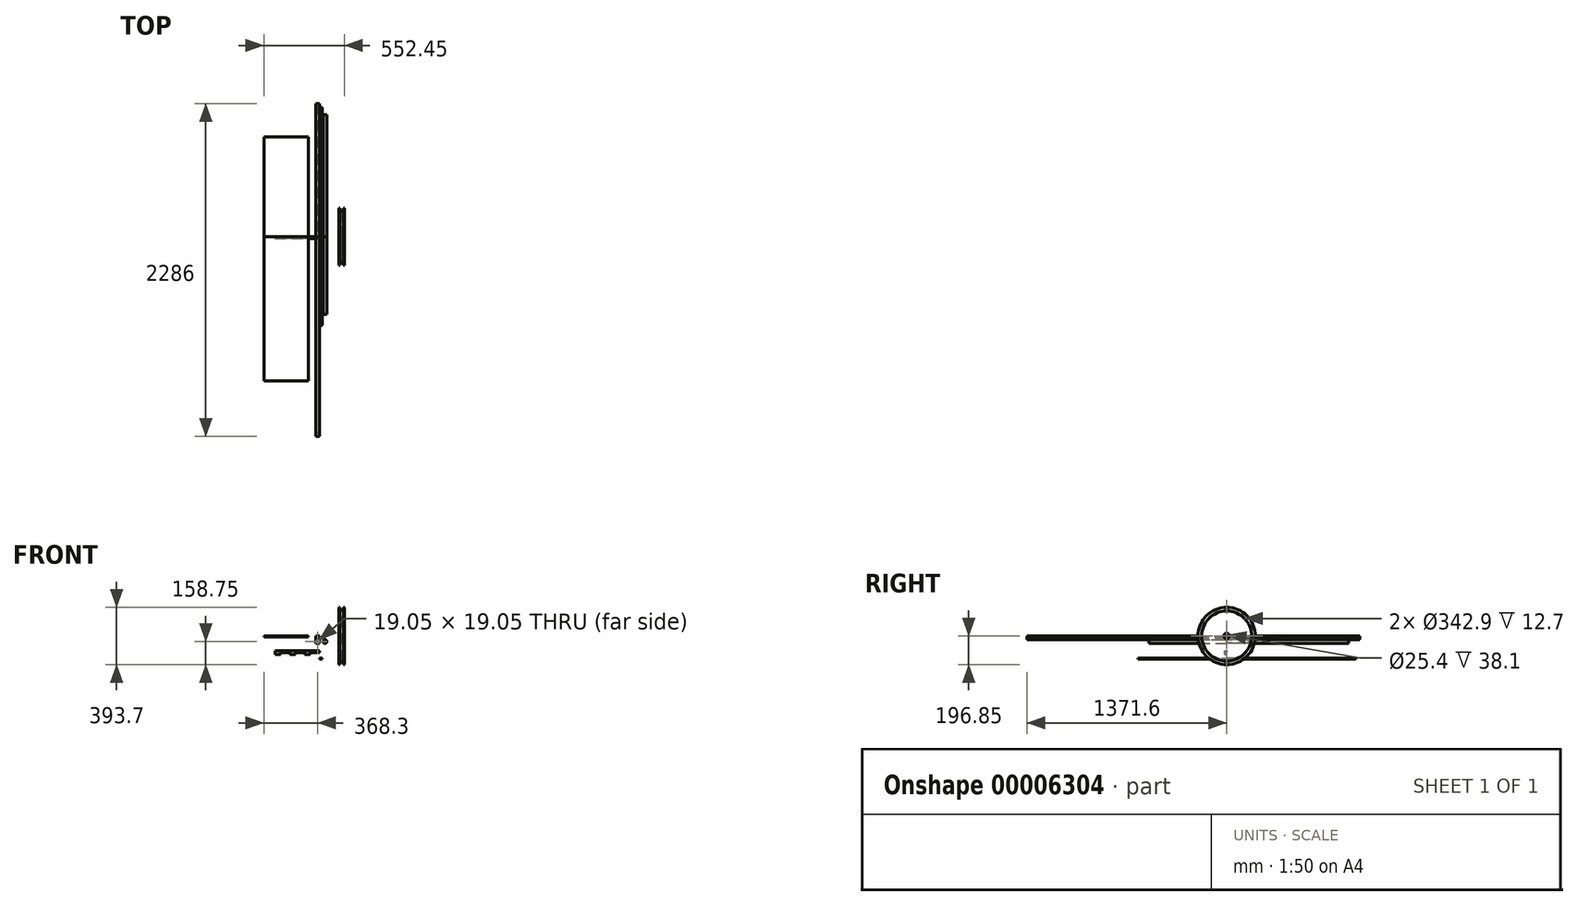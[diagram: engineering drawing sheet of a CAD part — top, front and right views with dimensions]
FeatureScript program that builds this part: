
annotation { "Feature Type Name" : "Feature", "Feature Type Description" : "" }
export const myFeature = defineFeature(function(context is Context, id is Id, definition is map)
    precondition{}
    {
        {
            var Q0;
            Q0=qCreatedBy(makeId("Front.planeOp"),FACE);
            var sketch = newSketch(context, id + "F0", { "sketchPlane" : qUnion([Q0])});
            skLineSegment(sketch, "E0", {"start": v(-25.4, 0) * mm, "end": v(-25.4, -25.4) * mm});
            skLineSegment(sketch, "E1", {"start": v(-25.4, -25.4) * mm, "end": v(-25.4, -25.4) * mm});
            skLineSegment(sketch, "E2", {"start": v(0, -19.05) * mm, "end": v(-19.05, -19.05) * mm});
            skLineSegment(sketch, "E3", {"start": v(-19.05, -25.4) * mm, "end": v(-19.05, -6.35) * mm});
            skLineSegment(sketch, "E4", {"start": v(-19.05, -6.35) * mm, "end": v(0, -6.35) * mm});
            skLineSegment(sketch, "E5", {"start": v(0, -25.4) * mm, "end": v(0, -19.05) * mm});
            skLineSegment(sketch, "E6", {"start": v(0, 0) * mm, "end": v(-25.4, 0) * mm});
            skLineSegment(sketch, "E7", {"start": v(0, 0) * mm, "end": v(0, -6.35) * mm});
            skLineSegment(sketch, "E8", {"start": v(-25.4, -25.4) * mm, "end": v(0, -25.4) * mm});
            skLineSegment(sketch, "E9", {"start": v(0, -25.4) * mm, "end": v(0, -50.8) * mm});
            skLineSegment(sketch, "E10", {"start": v(0, -50.8) * mm, "end": v(-25.4, -50.8) * mm});
            skLineSegment(sketch, "E11", {"start": v(-25.4, -50.8) * mm, "end": v(-25.4, -25.4) * mm});
            skLineSegment(sketch, "E12", {"start": v(-22.22, -28.57) * mm, "end": v(-22.22, -47.62) * mm});
            skLineSegment(sketch, "E13", {"start": v(-22.22, -47.62) * mm, "end": v(-3.17, -47.62) * mm});
            skLineSegment(sketch, "E14", {"start": v(-3.17, -47.62) * mm, "end": v(-3.18, -28.57) * mm});
            skLineSegment(sketch, "E15", {"start": v(-3.18, -28.57) * mm, "end": v(-22.22, -28.57) * mm});
            skCircle(sketch, "E16.0", {"center": v(38.1, -38.1) * mm, "radius": 12.7 * mm});
            skLineSegment(sketch, "E17.bottom", {"start": v(-76.2, 0) * mm, "end": v(-381, 0) * mm});
            skLineSegment(sketch, "E17.top", {"start": v(-76.2, -6.35) * mm, "end": v(-381, -6.35) * mm});
            skLineSegment(sketch, "E17.left", {"start": v(-76.2, 0) * mm, "end": v(-76.2, -6.35) * mm});
            skLineSegment(sketch, "E17.right", {"start": v(-381, 0) * mm, "end": v(-381, -6.35) * mm});
            skLineSegment(sketch, "E18", {"start": v(-304.8, -127) * mm, "end": v(-304.8, -101.6) * mm});
            skLineSegment(sketch, "E19", {"start": v(-304.8, -101.6) * mm, "end": v(0, -101.6) * mm});
            skLineSegment(sketch, "E20", {"start": v(0, -101.6) * mm, "end": v(0, -114.3) * mm});
            skLineSegment(sketch, "E21", {"start": v(0, -114.3) * mm, "end": v(-63.5, -114.3) * mm});
            skLineSegment(sketch, "E22", {"start": v(-63.5, -127) * mm, "end": v(-63.5, -114.3) * mm});
            skLineSegment(sketch, "E23", {"start": v(-63.5, -127) * mm, "end": v(-101.6, -127) * mm});
            skLineSegment(sketch, "E24", {"start": v(-101.6, -114.3) * mm, "end": v(-101.6, -127) * mm});
            skLineSegment(sketch, "E25", {"start": v(-101.6, -114.3) * mm, "end": v(-165.1, -114.3) * mm});
            skLineSegment(sketch, "E26", {"start": v(-165.1, -127) * mm, "end": v(-165.1, -114.3) * mm});
            skLineSegment(sketch, "E27", {"start": v(-165.1, -127) * mm, "end": v(-203.2, -127) * mm});
            skLineSegment(sketch, "E28", {"start": v(-203.2, -114.3) * mm, "end": v(-203.2, -127) * mm});
            skLineSegment(sketch, "E29", {"start": v(-203.2, -114.3) * mm, "end": v(-266.7, -114.3) * mm});
            skLineSegment(sketch, "E30", {"start": v(-266.7, -127) * mm, "end": v(-266.7, -114.3) * mm});
            skLineSegment(sketch, "E31", {"start": v(-266.7, -127) * mm, "end": v(-304.8, -127) * mm});
            skLineSegment(sketch, "E32.bottom", {"start": v(0, -152.4) * mm, "end": v(19.05, -152.4) * mm});
            skLineSegment(sketch, "E32.top", {"start": v(0, -158.75) * mm, "end": v(19.05, -158.75) * mm});
            skLineSegment(sketch, "E32.left", {"start": v(0, -152.4) * mm, "end": v(0, -158.75) * mm});
            skLineSegment(sketch, "E32.right", {"start": v(19.05, -152.4) * mm, "end": v(19.05, -158.75) * mm});
            skSolve(sketch);
        }
        {
            var Q0;
            {var subQ3=sQuery(id+"F0.wireOp",EDGE,"E0");Q0=makeQuery(id+"F0.imprint","IMPRINT",FACE,{"disambiguationData":[TD([[makeQuery(id+"F0.imprint","IMPRINT",EDGE,{"derivedFrom":subQ3}),1.0]])]});}
            extrude(context, id + "F1", {"entities" : qUnion([Q0]), "oppositeDirection" : true, "depth" : 914.4 * mm});
        }
        {
            var Q0;
            {var subQ3=sQuery(id+"F0.wireOp",EDGE,"E0");Q0=makeQuery(id+"F0.imprint","IMPRINT",FACE,{"disambiguationData":[TD([[makeQuery(id+"F0.imprint","IMPRINT",EDGE,{"derivedFrom":subQ3}),1.0]])]});}
            extrude(context, id + "F2", {"entities" : qUnion([Q0]), "depth" : 1371.6 * mm});
        }
        {
            var Q0;
            Q0=makeQuery(id+"F0.imprint","IMPRINT",FACE,{"disambiguationData":[TD([[makeQuery(id+"F0.imprint","IMPRINT",EDGE,{"derivedFrom":sQuery(id+"F0.wireOp",EDGE,"E32.bottom")}),-1.0]])]});
            extrude(context, id + "F3", {"entities" : qUnion([Q0]), "depth" : 609.6 * mm});
        }
        {
            var Q0;
            Q0=makeQuery(id+"F0.imprint","IMPRINT",FACE,{"disambiguationData":[TD([[makeQuery(id+"F0.imprint","IMPRINT",EDGE,{"derivedFrom":sQuery(id+"F0.wireOp",EDGE,"E32.bottom")}),-1.0]])]});
            var Q1;
            Q1=makeQuery(id+"F13.opRevolve","SWEPT_FACE",FACE,{"disambiguationData":[OSD([sQuery(id+"F12.wireOp",EDGE,"E49.0.MirrorCS")])]});
            extrude(context, id + "F4", {"entities" : qUnion([Q0, Q1]), "oppositeDirection" : true, "depth" : 889 * mm});
        }
        {
            var Q0;
            {var subQ4=sQuery(id+"F0.wireOp",EDGE,"E2");Q0=makeQuery(id+"F0.imprint","IMPRINT",FACE,{"disambiguationData":[TD([[makeQuery(id+"F0.imprint","IMPRINT",EDGE,{"derivedFrom":subQ4}),1.0]])]});}
            extrude(context, id + "F5", {"entities" : qUnion([Q0]), "oppositeDirection" : true, "depth" : 914.4 * mm});
        }
        {
            var Q0;
            {var subQ4=sQuery(id+"F0.wireOp",EDGE,"E2");Q0=makeQuery(id+"F0.imprint","IMPRINT",FACE,{"disambiguationData":[TD([[makeQuery(id+"F0.imprint","IMPRINT",EDGE,{"derivedFrom":subQ4}),1.0]])]});}
            extrude(context, id + "F6", {"entities" : qUnion([Q0]), "depth" : 1346.2 * mm});
        }
        {
            var Q0;
            {var subQ1=sQuery(id+"F0.wireOp",EDGE,"E9");Q0=makeQuery(id+"F0.imprint","IMPRINT",FACE,{"disambiguationData":[TD([[makeQuery(id+"F0.imprint","IMPRINT",EDGE,{"derivedFrom":subQ1}),-1.0]])]});}
            extrude(context, id + "F7", {"entities" : qUnion([Q0]), "oppositeDirection" : true, "depth" : 152.4 * mm});
        }
        {
            var Q0;
            Q0=makeQuery(id+"F0.imprint","IMPRINT",FACE,{"disambiguationData":[TD([[makeQuery(id+"F0.imprint","IMPRINT",EDGE,{"derivedFrom":sQuery(id+"F0.wireOp",EDGE,"E17.bottom")}),1.0]])]});
            extrude(context, id + "F8", {"entities" : qUnion([Q0]), "oppositeDirection" : true, "depth" : 685.8 * mm});
        }
        {
            var Q0;
            Q0=makeQuery(id+"F0.imprint","IMPRINT",FACE,{"disambiguationData":[TD([[makeQuery(id+"F0.imprint","IMPRINT",EDGE,{"derivedFrom":sQuery(id+"F0.wireOp",EDGE,"E17.bottom")}),1.0]])]});
            var Q1;
            Q1=sQuery(id+"F0.wireOp",EDGE,"E17.top");
            extrude(context, id + "F9", {"entities" : qUnion([Q0]), "surfaceEntities" : qUnion([Q1]), "depth" : 990.6 * mm});
        }
        {
            var Q0;
            Q0=makeQuery(id+"F0.imprint","IMPRINT",FACE,{"disambiguationData":[TD([[makeQuery(id+"F0.imprint","IMPRINT",EDGE,{"derivedFrom":sQuery(id+"F0.wireOp",EDGE,"E16.0")}),1.0]])]});
            extrude(context, id + "F10", {"entities" : qUnion([Q0]), "oppositeDirection" : true, "depth" : 838.2 * mm});
        }
        {
            var Q0;
            Q0=makeQuery(id+"F0.imprint","IMPRINT",FACE,{"disambiguationData":[TD([[makeQuery(id+"F0.imprint","IMPRINT",EDGE,{"derivedFrom":sQuery(id+"F0.wireOp",EDGE,"E16.0")}),1.0]])]});
            extrude(context, id + "F11", {"entities" : qUnion([Q0]), "depth" : 533.4 * mm});
        }
        {
            var Q0;
            Q0=qCreatedBy(makeId("Top.planeOp"),FACE);
            var sketch = newSketch(context, id + "F12", { "sketchPlane" : qUnion([Q0])});
            skLineSegment(sketch, "E33", {"start": v(146.05, 19.05) * mm, "end": v(146.05, 171.45) * mm});
            skLineSegment(sketch, "E34", {"start": v(152.4, 177.8) * mm, "end": v(152.4, 0) * mm, "construction": true});
            skLineSegment(sketch, "E35", {"start": v(152.4, 0) * mm, "end": v(0, 0) * mm, "construction": true});
            skLineSegment(sketch, "E36", {"start": v(152.4, 177.8) * mm, "end": v(139.7, 177.8) * mm});
            skLineSegment(sketch, "E37", {"start": v(139.7, 177.8) * mm, "end": v(139.7, 196.85) * mm});
            skLineSegment(sketch, "E38", {"start": v(139.7, 196.85) * mm, "end": v(133.35, 196.85) * mm});
            skLineSegment(sketch, "E39", {"start": v(133.35, 196.85) * mm, "end": v(133.35, 171.45) * mm});
            skLineSegment(sketch, "E40", {"start": v(133.35, 171.45) * mm, "end": v(146.05, 171.45) * mm});
            skLineSegment(sketch, "E41", {"start": v(133.35, 19.05) * mm, "end": v(133.35, 12.7) * mm});
            skLineSegment(sketch, "E42", {"start": v(133.35, 19.05) * mm, "end": v(146.05, 19.05) * mm});
            skLineSegment(sketch, "E43", {"start": v(133.35, 12.7) * mm, "end": v(152.4, 12.7) * mm});
            skLineSegment(sketch, "E44.0.MirrorCS", {"start": v(152.4, 177.8) * mm, "end": v(165.1, 177.8) * mm});
            skLineSegment(sketch, "E45.0.MirrorCS", {"start": v(165.1, 177.8) * mm, "end": v(165.1, 196.85) * mm});
            skLineSegment(sketch, "E46.0.MirrorCS", {"start": v(165.1, 196.85) * mm, "end": v(171.45, 196.85) * mm});
            skLineSegment(sketch, "E47.0.MirrorCS", {"start": v(171.45, 196.85) * mm, "end": v(171.45, 171.45) * mm});
            skLineSegment(sketch, "E48.0.MirrorCS", {"start": v(171.45, 171.45) * mm, "end": v(158.75, 171.45) * mm});
            skLineSegment(sketch, "E49.0.MirrorCS", {"start": v(158.75, 19.05) * mm, "end": v(158.75, 171.45) * mm});
            skLineSegment(sketch, "E50.0.MirrorCS", {"start": v(171.45, 19.05) * mm, "end": v(158.75, 19.05) * mm});
            skLineSegment(sketch, "E51.0.MirrorCS", {"start": v(171.45, 19.05) * mm, "end": v(171.45, 12.7) * mm});
            skLineSegment(sketch, "E52.0.MirrorCS", {"start": v(171.45, 12.7) * mm, "end": v(152.4, 12.7) * mm});
            skSolve(sketch);
        }
        {
            var Q0;
            Q0=makeQuery(id+"F12.imprint","IMPRINT",FACE,{"disambiguationData":[TD([[makeQuery(id+"F12.imprint","IMPRINT",EDGE,{"derivedFrom":sQuery(id+"F12.wireOp",EDGE,"E33")}),-1.0]])]});
            var Q1;
            Q1=sQuery(id+"F12.wireOp",EDGE,"E35");
            revolve(context, id + "F13", {"entities" : qUnion([Q0]), "axis" : qUnion([Q1]), "revolveType" : RevolveType.FULL});
        }
        {
            var Q0;
            Q0=makeQuery(id+"F0.imprint","IMPRINT",FACE,{"disambiguationData":[TD([[makeQuery(id+"F0.imprint","IMPRINT",EDGE,{"derivedFrom":sQuery(id+"F0.wireOp",EDGE,"E18")}),-1.0]])]});
            extrude(context, id + "F14", {"entities" : qUnion([Q0]), "depth" : 12.7 * mm});
        }
    });
